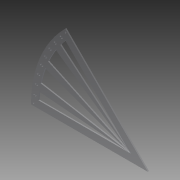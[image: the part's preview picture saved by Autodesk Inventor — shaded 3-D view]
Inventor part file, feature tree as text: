
AUTODESK INVENTOR PART (.ipt)
format: ipt  version: 2013 (Build 170138000, 138)  size: 170,496 bytes
history: native  units: in
note: dims shown in document units (in); Inventor stores cm internally (conversion verified against a paired STEP export)
features: extrude x4, sketch x4
ambient origin geometry x8: Origin, YZ Plane, XZ Plane, XY Plane, X Axis, Y Axis, Z Axis, Center Point
bodies: Solid1 (feature_tree)
feature tree (8):
  extrude  "Extrusion1"  Depth=0.375in
  extrude  "Extrusion2"  Depth=0.0625in
  extrude  "Extrusion4"  Depth=3.937in TaperAngle=45.0deg
  extrude  "Extrusion5"  Depth=0.125in
  sketch  "Sketch1"  dims[d0=0.125in d1=0.0in d2=0.375in]
  sketch  "Sketch4"  dims[d3=0.0625in d4=0.0625in]
  sketch  "Sketch7"  dims[d5=0.0625in d6=3.937in d8=45.0deg]
  sketch  "Sketch9"  dims[d10=0.25in d13=0.125in d14=0.25in d15=1.0in d16=0.0in d29=6.0in d31=0.125in d32=0.0in d34=0.75in d35=1.0in d36=1.0in d38=1.0in d39=1.0in d40=1.0in d41=1.0in d44=0.125in d45=0.0in]
